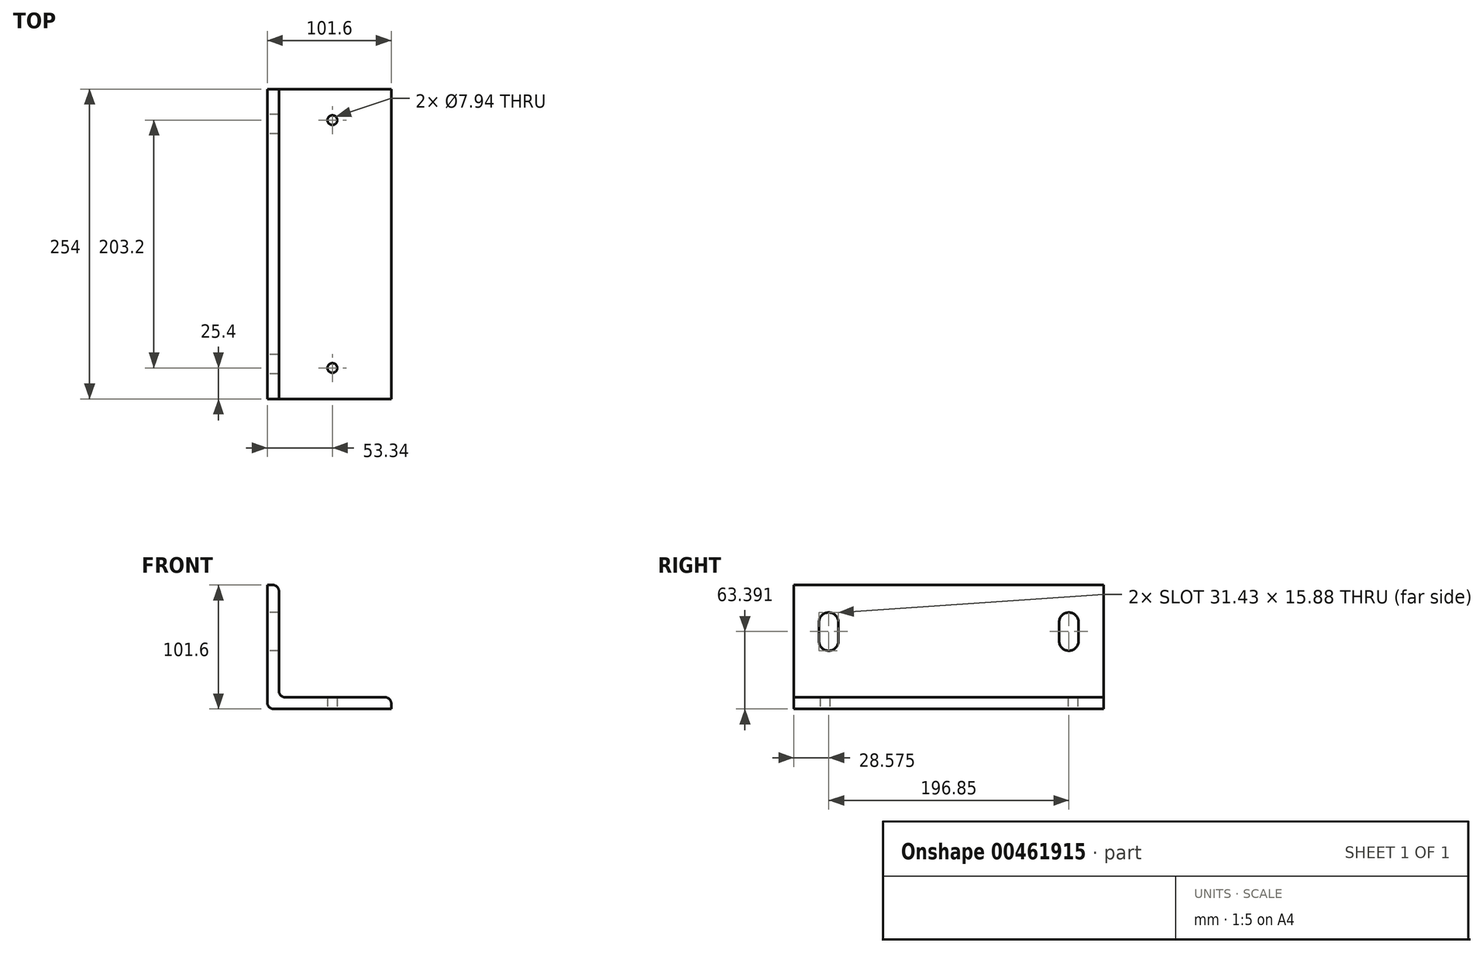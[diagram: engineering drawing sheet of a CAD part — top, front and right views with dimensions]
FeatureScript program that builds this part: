
annotation { "Feature Type Name" : "Feature", "Feature Type Description" : "" }
export const myFeature = defineFeature(function(context is Context, id is Id, definition is map)
    precondition{}
    {
        {
            var Q0;
            Q0=qCreatedBy(makeId("Front.planeOp"),FACE);
            var sketch = newSketch(context, id + "F0", { "sketchPlane" : qUnion([Q0])});
            skLineSegment(sketch, "E0", {"start": v(0, 0) * mm, "end": v(0, 101.6) * mm});
            skLineSegment(sketch, "E1", {"start": v(0, 101.6) * mm, "end": v(9.53, 101.6) * mm});
            skLineSegment(sketch, "E2", {"start": v(9.53, 101.6) * mm, "end": v(9.53, 9.53) * mm});
            skLineSegment(sketch, "E3", {"start": v(9.52, 9.53) * mm, "end": v(101.6, 9.53) * mm});
            skLineSegment(sketch, "E4", {"start": v(101.6, 9.53) * mm, "end": v(101.6, 0) * mm});
            skLineSegment(sketch, "E5", {"start": v(101.6, 0) * mm, "end": v(0, 0) * mm});
            skSolve(sketch);
        }
        {
            var Q0;
            Q0 = qSketchRegion(id + "F0", true);
            extrude(context, id + "F1", {"entities" : qUnion([Q0]), "endBound" : BoundingType.SYMMETRIC, "depth" : 254 * mm});
        }
        {
            var Q0;
            Q0=makeQuery(id+"F1.opExtrude","SWEPT_EDGE",EDGE,{"disambiguationData":[OSD([sQuery(id+"F0.wireOp",EDGE,"E2"),sQuery(id+"F0.wireOp",EDGE,"E3")])]});
            var Q1;
            Q1=makeQuery(id+"F1.opExtrude","SWEPT_EDGE",EDGE,{"disambiguationData":[OSD([sQuery(id+"F0.wireOp",EDGE,"E0"),sQuery(id+"F0.wireOp",EDGE,"E5")])]});
            var Q2;
            Q2=makeQuery(id+"F1.opExtrude","SWEPT_EDGE",EDGE,{"disambiguationData":[OSD([sQuery(id+"F0.wireOp",EDGE,"E1"),sQuery(id+"F0.wireOp",EDGE,"E2")])]});
            var Q3;
            Q3=makeQuery(id+"F1.opExtrude","SWEPT_EDGE",EDGE,{"disambiguationData":[OSD([sQuery(id+"F0.wireOp",EDGE,"E3"),sQuery(id+"F0.wireOp",EDGE,"E4")])]});
            fillet(context, id + "F2", {"entities" : qUnion([Q0, Q1, Q2, Q3]), "radius" : 5.08 * mm, "tangentPropagation" : true, "allowEdgeOverflow" : false});
        }
        {
            var Q0;
            Q0=makeQuery(id+"F1.opExtrude","SWEPT_FACE",FACE,{"disambiguationData":[OSD([sQuery(id+"F0.wireOp",EDGE,"E0")])]});
            var sketch = newSketch(context, id + "F3", { "sketchPlane" : qUnion([Q0])});
            skArc(sketch, "E6", {"start": v(-90.49, 71.17) * mm, "mid": v(-98.43, 79.1) * mm, "end": v(-106.36, 71.17) * mm});
            skArc(sketch, "E7", {"start": v(-106.36, 55.61) * mm, "mid": v(-98.43, 47.68) * mm, "end": v(-90.49, 55.61) * mm});
            skLineSegment(sketch, "E8", {"start": v(-106.36, 55.61) * mm, "end": v(-106.36, 71.17) * mm});
            skLineSegment(sketch, "E9", {"start": v(-90.49, 71.17) * mm, "end": v(-90.49, 55.61) * mm});
            skPoint(sketch, "E10.center.orphan", {"position": v(-98.43, 63.4) * mm});
            skArc(sketch, "E11.MirrorCS", {"start": v(106.36, 55.61) * mm, "mid": v(98.43, 47.68) * mm, "end": v(90.49, 55.61) * mm});
            skArc(sketch, "E12.MirrorCS", {"start": v(90.49, 71.17) * mm, "mid": v(98.43, 79.1) * mm, "end": v(106.36, 71.17) * mm});
            skLineSegment(sketch, "E13.MirrorCS", {"start": v(106.36, 55.61) * mm, "end": v(106.36, 71.17) * mm});
            skPoint(sketch, "E14.MirrorP", {"position": v(98.43, 63.4) * mm});
            skLineSegment(sketch, "E15.MirrorCS", {"start": v(90.49, 71.17) * mm, "end": v(90.49, 55.61) * mm});
            skSolve(sketch);
        }
        {
            var Q0;
            Q0 = qSketchRegion(id + "F3", true);
            extrude(context, id + "F4", {"entities" : qUnion([Q0]), "operationType" : NewBodyOperationType.REMOVE, "oppositeDirection" : true, "depth" : 25.4 * mm});
        }
        {
            var Q0;
            Q0=makeQuery(id+"F1.opExtrude","SWEPT_FACE",FACE,{"disambiguationData":[OSD([sQuery(id+"F0.wireOp",EDGE,"E5")])]});
            var sketch = newSketch(context, id + "F5", { "sketchPlane" : qUnion([Q0])});
            skCircle(sketch, "E16", {"center": v(53.34, 101.6) * mm, "radius": 3.97 * mm});
            skPoint(sketch, "E16.centerSnap0", {"position": v(53.34, 127) * mm});
            skCircle(sketch, "E17.MirrorC", {"center": v(53.34, -101.6) * mm, "radius": 3.97 * mm});
            skSolve(sketch);
        }
        {
            var Q0;
            Q0 = qSketchRegion(id + "F5", true);
            extrude(context, id + "F6", {"entities" : qUnion([Q0]), "operationType" : NewBodyOperationType.REMOVE, "oppositeDirection" : true, "depth" : 25.4 * mm});
        }
    });
